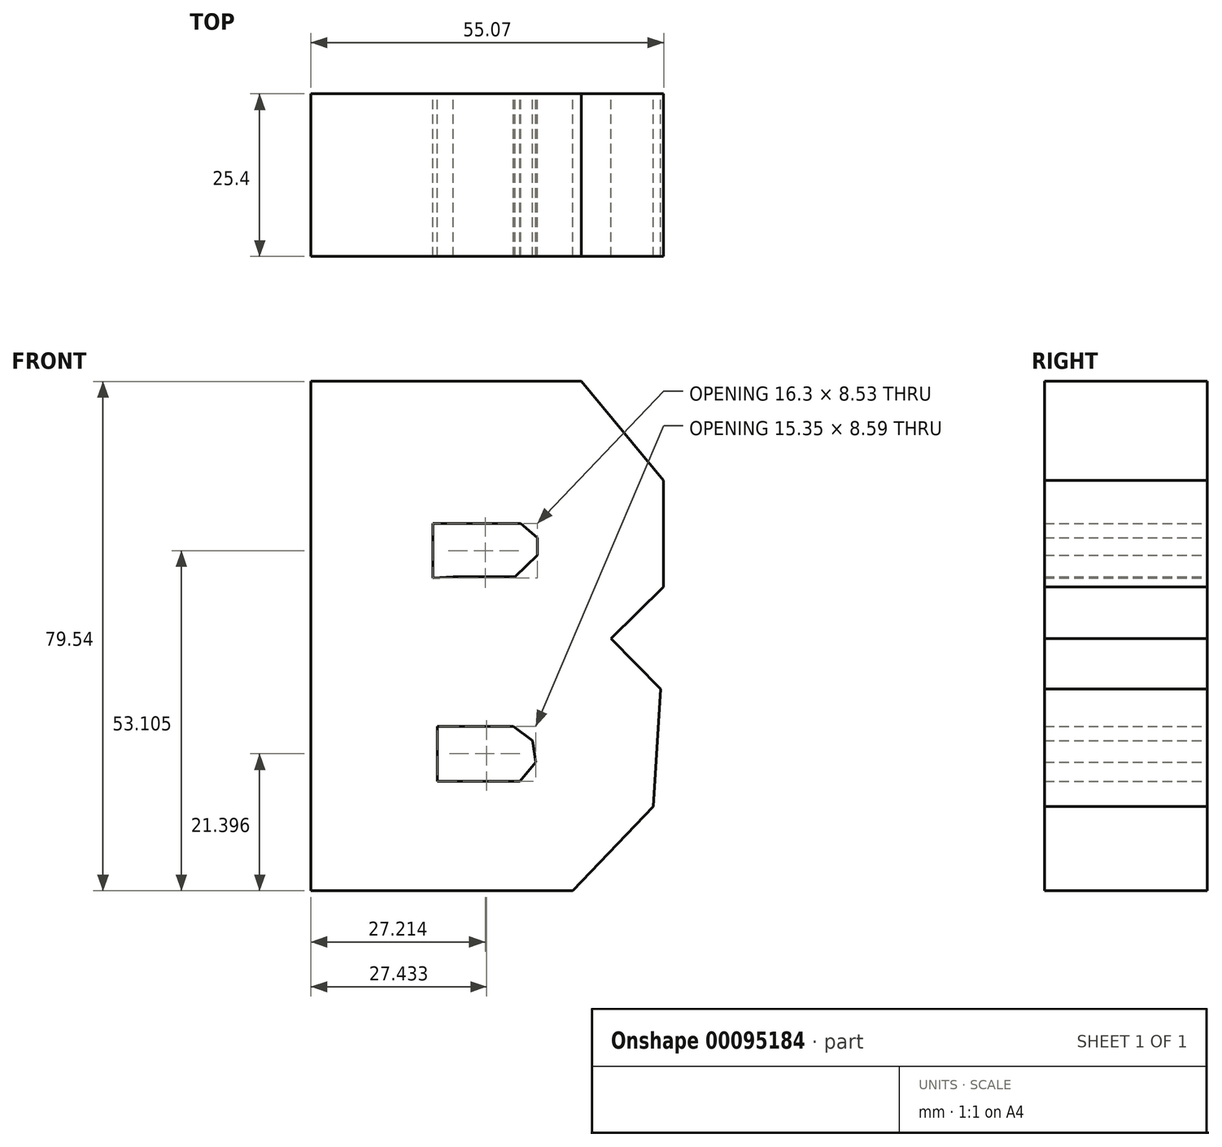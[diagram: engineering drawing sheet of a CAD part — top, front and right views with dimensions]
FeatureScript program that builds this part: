
annotation { "Feature Type Name" : "Feature", "Feature Type Description" : "" }
export const myFeature = defineFeature(function(context is Context, id is Id, definition is map)
    precondition{}
    {
        {
            var Q0;
            Q0=qCreatedBy(makeId("Front.planeOp"),FACE);
            var sketch = newSketch(context, id + "F0", { "sketchPlane" : qUnion([Q0])});
            skFitSpline(sketch, "E0", {"points": [v(-44.8, 52.5) * mm, v(-57.42, 34.39) * mm, v(-63.45, 19.8) * mm, v(-66, -6.02) * mm, v(-60.47, -27.56) * mm, v(-44.37, -49.27) * mm, v(-17.57, -64.69) * mm, v(16.1, -66.12) * mm, v(43.5, -53.34) * mm, v(59.1, -35.99) * mm, v(68.55, -12.58) * mm, v(67.76, 21.74) * mm, v(53.8, 48.36) * mm, v(37.88, 61.58) * mm], "startDerivative": vector(-197.17, -267.74) * mm, "endDerivative": vector(-227.1, 131.24) * mm});
            skFitSpline(sketch, "E1", {"points": [v(37.88, 61.58) * mm, v(8.31, 69.6) * mm, v(-32.51, 61.58) * mm, v(-44.8, 52.5) * mm], "startDerivative": vector(-78.32, 31.4) * mm, "endDerivative": vector(-45.95, -32.91) * mm});
            skLineSegment(sketch, "E2", {"start": v(-4.04, 60.78) * mm, "end": v(-4.04, 47.57) * mm});
            skLineSegment(sketch, "E3", {"start": v(-4.04, 47.57) * mm, "end": v(-28.75, 47.57) * mm});
            skLineSegment(sketch, "E4", {"start": v(-28.75, 47.57) * mm, "end": v(-28.75, 38.04) * mm});
            skLineSegment(sketch, "E5", {"start": v(-28.75, 38.04) * mm, "end": v(-41.03, 55.2) * mm});
            skLineSegment(sketch, "E6", {"start": v(-48.98, 46.9) * mm, "end": v(-30.56, 26) * mm});
            skLineSegment(sketch, "E7", {"start": v(-30.56, 26) * mm, "end": v(-30.56, 8.92) * mm});
            skLineSegment(sketch, "E8", {"start": v(-30.56, 8.92) * mm, "end": v(-65.4, 8.92) * mm});
            skLineSegment(sketch, "E9", {"start": v(-66.1, -3.1) * mm, "end": v(-29.8, -3.1) * mm});
            skLineSegment(sketch, "E10", {"start": v(-29.8, -3.1) * mm, "end": v(-29.8, -20.8) * mm});
            skLineSegment(sketch, "E11", {"start": v(-29.8, -20.8) * mm, "end": v(-50.96, -41.4) * mm});
            skLineSegment(sketch, "E12", {"start": v(-44.37, -49.27) * mm, "end": v(-30.35, -34.51) * mm});
            skLineSegment(sketch, "E13", {"start": v(-30.35, -34.51) * mm, "end": v(-30.35, -42.66) * mm});
            skLineSegment(sketch, "E14", {"start": v(-30.35, -42.66) * mm, "end": v(-5.47, -42.66) * mm});
            skLineSegment(sketch, "E15", {"start": v(-5.47, -42.66) * mm, "end": v(-5.47, -67.12) * mm});
            skLineSegment(sketch, "E16", {"start": v(5.79, -69.4) * mm, "end": v(5.79, -42.54) * mm});
            skLineSegment(sketch, "E17", {"start": v(5.79, -42.54) * mm, "end": v(20.27, -42.54) * mm});
            skLineSegment(sketch, "E18", {"start": v(20.27, -42.54) * mm, "end": v(29.74, -32.79) * mm});
            skLineSegment(sketch, "E19", {"start": v(29.74, -32.79) * mm, "end": v(47.47, -50) * mm});
            skLineSegment(sketch, "E20", {"start": v(54.06, -42.67) * mm, "end": v(36.66, -26.7) * mm});
            skLineSegment(sketch, "E21", {"start": v(69.98, 6.06) * mm, "end": v(36.35, 5.81) * mm});
            skLineSegment(sketch, "E22", {"start": v(36.35, 5.81) * mm, "end": v(36.31, 10.38) * mm});
            skLineSegment(sketch, "E23", {"start": v(36.31, 10.38) * mm, "end": v(36.31, 29.28) * mm});
            skLineSegment(sketch, "E24", {"start": v(30.36, 39.93) * mm, "end": v(20.42, 46.7) * mm});
            skLineSegment(sketch, "E25", {"start": v(20.42, 46.7) * mm, "end": v(8.43, 46.7) * mm});
            skLineSegment(sketch, "E26", {"start": v(8.43, 46.7) * mm, "end": v(8.31, 69.6) * mm});
            skLineSegment(sketch, "E27", {"start": v(-4.04, 60.78) * mm, "end": v(-4.04, 69.16) * mm});
            skLineSegment(sketch, "E28", {"start": v(36.66, -26.7) * mm, "end": v(36.66, -4.7) * mm});
            skLineSegment(sketch, "E29", {"start": v(36.66, -4.7) * mm, "end": v(69.69, -4.7) * mm});
            skLineSegment(sketch, "E30", {"start": v(31.21, -22.63) * mm, "end": v(18.65, -35.76) * mm});
            skLineSegment(sketch, "E31", {"start": v(18.65, -35.76) * mm, "end": v(-22.23, -35.76) * mm});
            skLineSegment(sketch, "E32", {"start": v(-22.23, -35.76) * mm, "end": v(-22.23, 43.78) * mm});
            skLineSegment(sketch, "E33", {"start": v(-22.23, 43.78) * mm, "end": v(20, 43.78) * mm});
            skLineSegment(sketch, "E34", {"start": v(20, 43.78) * mm, "end": v(32.84, 28.3) * mm});
            skLineSegment(sketch, "E35", {"start": v(32.84, 28.3) * mm, "end": v(32.84, 11.68) * mm});
            skLineSegment(sketch, "E36", {"start": v(32.84, 11.68) * mm, "end": v(24.62, 3.62) * mm});
            skLineSegment(sketch, "E37", {"start": v(24.62, 3.62) * mm, "end": v(32.34, -4.24) * mm});
            skLineSegment(sketch, "E38", {"start": v(32.34, -4.24) * mm, "end": v(31.21, -22.63) * mm});
            skLineSegment(sketch, "E39", {"start": v(0, 13.28) * mm, "end": v(9.66, 13.28) * mm});
            skLineSegment(sketch, "E40", {"start": v(9.66, 13.28) * mm, "end": v(13.14, 16.64) * mm});
            skLineSegment(sketch, "E41", {"start": v(13.14, 16.64) * mm, "end": v(13.14, 19.37) * mm});
            skLineSegment(sketch, "E42", {"start": v(13.14, 19.37) * mm, "end": v(10.5, 21.6) * mm});
            skLineSegment(sketch, "E43", {"start": v(10.5, 21.6) * mm, "end": v(-3.17, 21.6) * mm});
            skLineSegment(sketch, "E44", {"start": v(-3.17, 21.6) * mm, "end": v(-3.17, 13.08) * mm});
            skLineSegment(sketch, "E45", {"start": v(-3.17, 13.08) * mm, "end": v(0, 13.28) * mm});
            skLineSegment(sketch, "E46", {"start": v(12.88, -15.7) * mm, "end": v(10.38, -18.66) * mm});
            skLineSegment(sketch, "E47", {"start": v(10.38, -18.66) * mm, "end": v(0.7, -18.66) * mm});
            skLineSegment(sketch, "E48", {"start": v(0.7, -18.66) * mm, "end": v(-2.47, -18.66) * mm});
            skLineSegment(sketch, "E49", {"start": v(-2.47, -18.66) * mm, "end": v(-2.47, -10.07) * mm});
            skLineSegment(sketch, "E50", {"start": v(-2.47, -10.07) * mm, "end": v(9.4, -10.07) * mm});
            skLineSegment(sketch, "E51", {"start": v(9.4, -10.07) * mm, "end": v(12.37, -12.32) * mm});
            skLineSegment(sketch, "E52", {"start": v(12.37, -12.32) * mm, "end": v(12.88, -15.7) * mm});
            skSolve(sketch);
        }
        {
            var Q0;
            Q0=makeQuery(id+"F0.imprint","IMPRINT",FACE,{"disambiguationData":[TD([[makeQuery(id+"F0.imprint","IMPRINT",EDGE,{"derivedFrom":sQuery(id+"F0.wireOp",EDGE,"E30")}),-1.0]])]});
            extrude(context, id + "F1", {"entities" : qUnion([Q0]), "depth" : 25.4 * mm});
        }
    });
